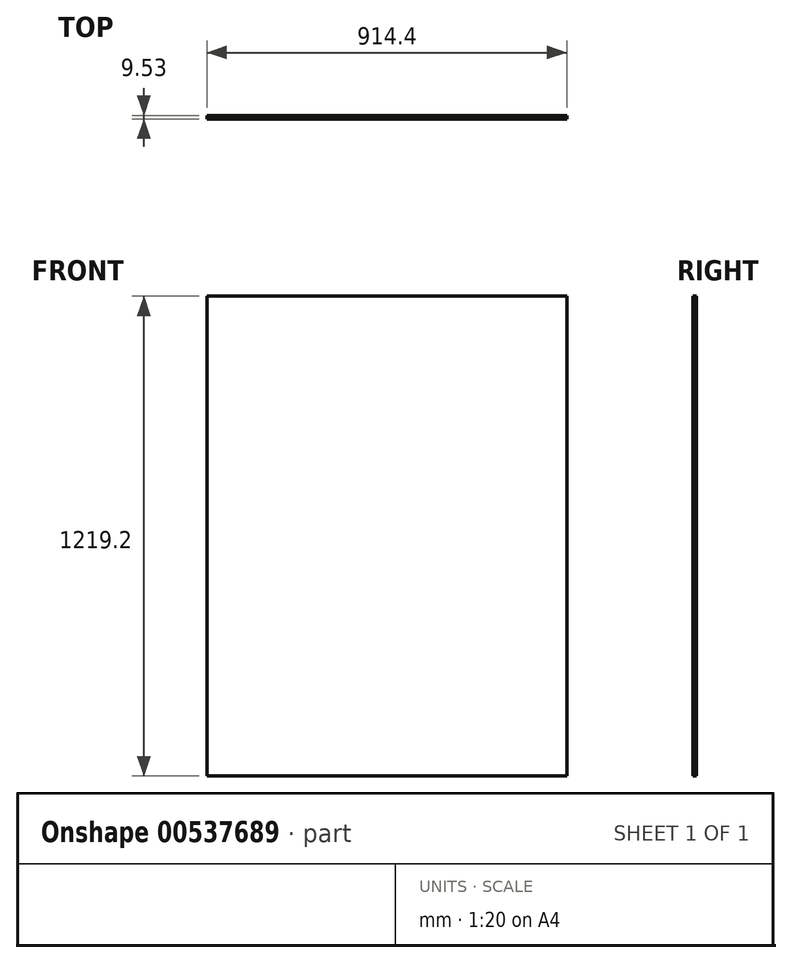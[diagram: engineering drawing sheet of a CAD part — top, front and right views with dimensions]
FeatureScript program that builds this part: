
annotation { "Feature Type Name" : "Feature", "Feature Type Description" : "" }
export const myFeature = defineFeature(function(context is Context, id is Id, definition is map)
    precondition{}
    {
        {
            var Q0;
            Q0=qCreatedBy(makeId("Front.planeOp"),FACE);
            var sketch = newSketch(context, id + "F0", { "sketchPlane" : qUnion([Q0])});
            skLineSegment(sketch, "E0.bottom", {"start": v(457.2, 609.6) * mm, "end": v(-457.2, 609.6) * mm});
            skLineSegment(sketch, "E0.top", {"start": v(457.2, -609.6) * mm, "end": v(-457.2, -609.6) * mm});
            skLineSegment(sketch, "E0.left", {"start": v(457.2, 609.6) * mm, "end": v(457.2, -609.6) * mm});
            skLineSegment(sketch, "E0.right", {"start": v(-457.2, 609.6) * mm, "end": v(-457.2, -609.6) * mm});
            skPoint(sketch, "E0.middle", {"position": v(0, 0) * mm});
            skSolve(sketch);
        }
        {
            var Q0;
            Q0 = qSketchRegion(id + "F0", true);
            extrude(context, id + "F1", {"entities" : qUnion([Q0]), "depth" : 9.52 * mm, "offsetDistance" : 25.4 * mm});
        }
    });
